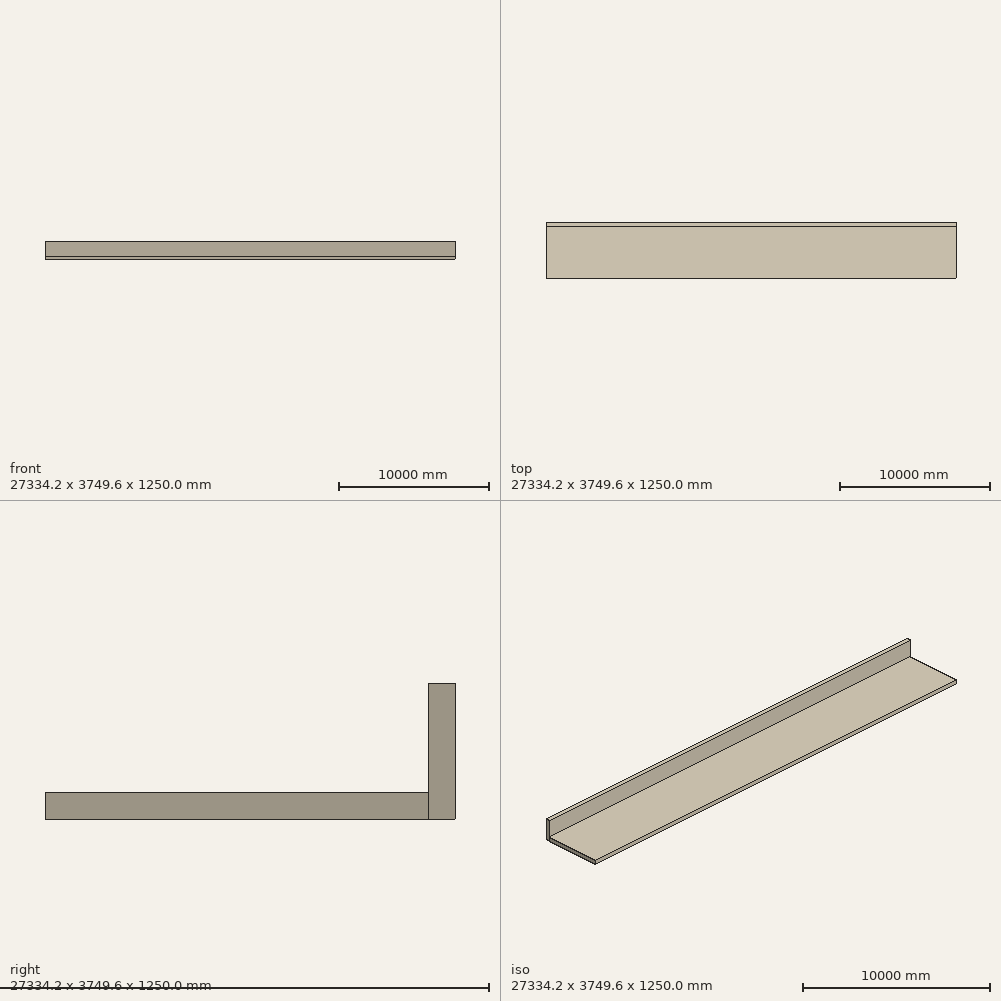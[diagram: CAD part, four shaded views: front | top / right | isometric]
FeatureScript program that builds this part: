
annotation { "Feature Type Name" : "Feature", "Feature Type Description" : "" }
export const myFeature = defineFeature(function(context is Context, id is Id, definition is map)
    precondition{}
    {
        {
            var Q0;
            Q0=qCreatedBy(makeId("Top.planeOp"),FACE);
            var sketch = newSketch(context, id + "F0", { "sketchPlane" : qUnion([Q0])});
            skLineSegment(sketch, "E0.bottom", {"start": v(-13653.67, -3086.65) * mm, "end": v(13646.33, -3086.65) * mm});
            skLineSegment(sketch, "E0.top", {"start": v(-13653.67, -6586.65) * mm, "end": v(13646.33, -6586.65) * mm});
            skLineSegment(sketch, "E0.left", {"start": v(-13653.67, -3086.65) * mm, "end": v(-13653.67, -6586.65) * mm});
            skLineSegment(sketch, "E0.right", {"start": v(13646.33, -3086.65) * mm, "end": v(13646.33, -6586.65) * mm});
            skSolve(sketch);
        }
        {
            var Q0;
            Q0=qCreatedBy(makeId("Top.planeOp"),FACE);
            var sketch = newSketch(context, id + "F1", { "sketchPlane" : qUnion([Q0])});
            skLineSegment(sketch, "E1.bottom", {"start": v(-13619.48, -3087.02) * mm, "end": v(13680.52, -3087.02) * mm});
            skLineSegment(sketch, "E1.top", {"start": v(-13619.48, -2837.02) * mm, "end": v(13680.52, -2837.02) * mm});
            skLineSegment(sketch, "E1.left", {"start": v(-13619.48, -3087.02) * mm, "end": v(-13619.48, -2837.02) * mm});
            skLineSegment(sketch, "E1.right", {"start": v(13680.52, -3087.02) * mm, "end": v(13680.52, -2837.02) * mm});
            skSolve(sketch);
        }
        {
            var Q0;
            Q0 = qSketchRegion(id + "F0", true);
            extrude(context, id + "F2", {"entities" : qUnion([Q0]), "oppositeDirection" : true, "depth" : 250 * mm});
        }
        {
            var Q0;
            Q0 = qSketchRegion(id + "F1", true);
            extrude(context, id + "F3", {"entities" : qUnion([Q0]), "depth" : 1000 * mm, "hasSecondDirection" : true, "secondDirectionOppositeDirection" : true, "secondDirectionDepth" : 250 * mm});
        }
    });
